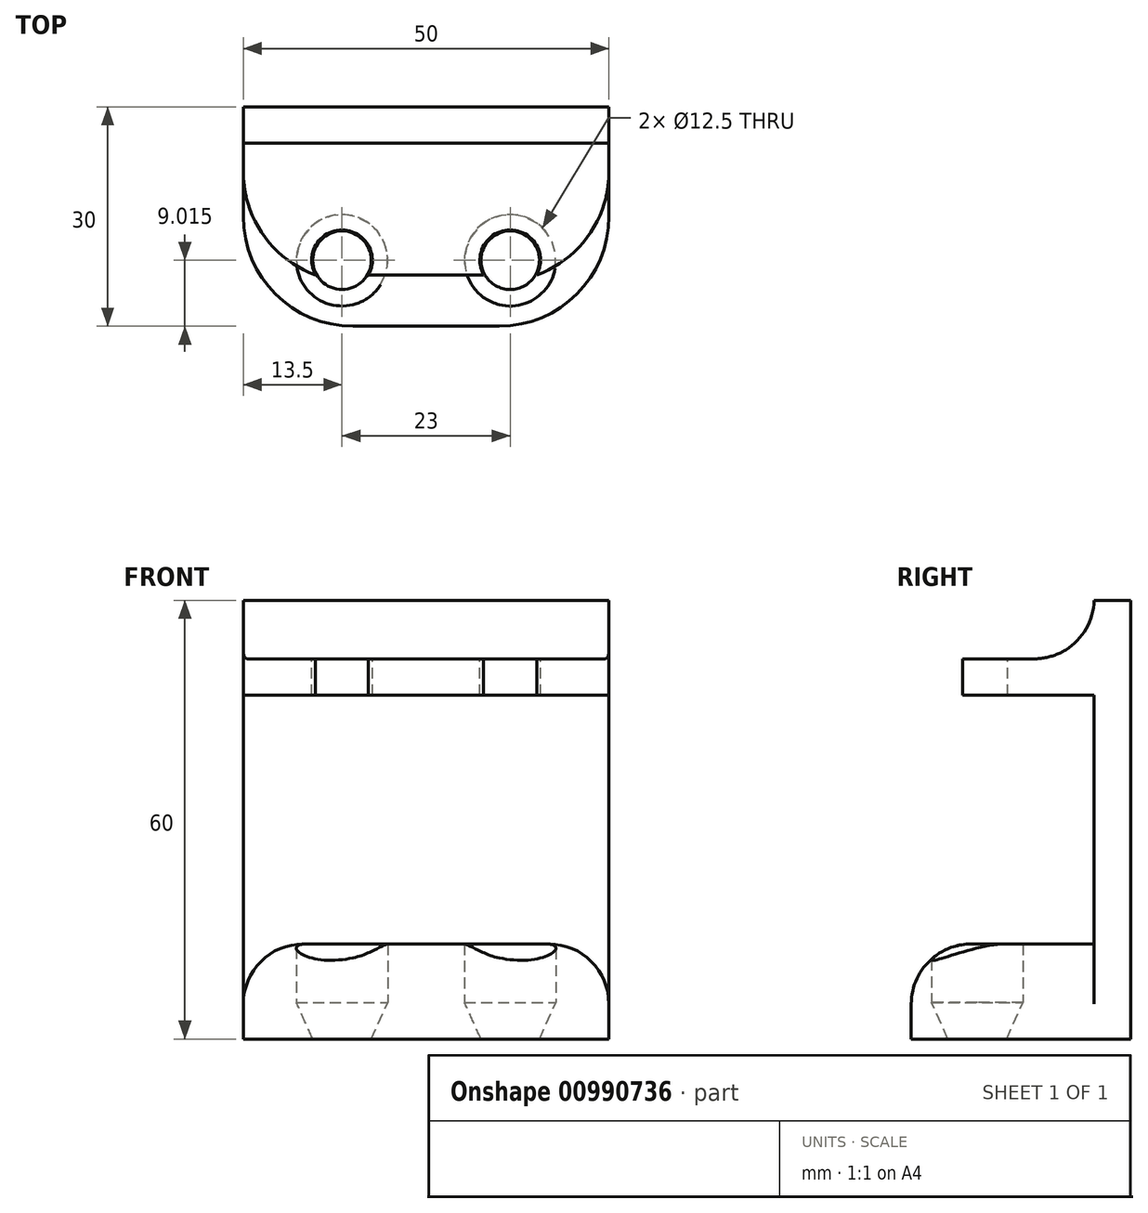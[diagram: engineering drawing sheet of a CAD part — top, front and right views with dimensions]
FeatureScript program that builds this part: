
annotation { "Feature Type Name" : "Feature", "Feature Type Description" : "" }
export const myFeature = defineFeature(function(context is Context, id is Id, definition is map)
    precondition{}
    {
        {
            var Q0;
            Q0=qCreatedBy(makeId("Front.planeOp"),FACE);
            var sketch = newSketch(context, id + "F0", { "sketchPlane" : qUnion([Q0])});
            skLineSegment(sketch, "E0.bottom", {"start": v(-25, 0) * mm, "end": v(25, 0) * mm});
            skLineSegment(sketch, "E0.top", {"start": v(-25, 60) * mm, "end": v(25, 60) * mm});
            skLineSegment(sketch, "E0.left", {"start": v(-25, 0) * mm, "end": v(-25, 60) * mm});
            skLineSegment(sketch, "E0.right", {"start": v(25, 0) * mm, "end": v(25, 60) * mm});
            skSolve(sketch);
        }
        {
            var Q0;
            Q0 = qSketchRegion(id + "F0", true);
            extrude(context, id + "F1", {"entities" : qUnion([Q0]), "depth" : 5 * mm, "offsetDistance" : 25 * mm});
        }
        {
            var Q0;
            Q0=makeQuery(id+"F1.opExtrude","CAP_FACE",FACE,{"disambiguationData":[OSD([sQuery(id+"F0.wireOp",EDGE,"E0.bottom"),sQuery(id+"F0.wireOp",EDGE,"E0.top"),sQuery(id+"F0.wireOp",EDGE,"E0.left"),sQuery(id+"F0.wireOp",EDGE,"E0.right")])],"isStart":false});
            var sketch = newSketch(context, id + "F2", { "sketchPlane" : qUnion([Q0])});
            skLineSegment(sketch, "E1.bottom", {"start": v(-25, 0) * mm, "end": v(25, 0) * mm});
            skLineSegment(sketch, "E1.top", {"start": v(-25, 5) * mm, "end": v(25, 5) * mm});
            skLineSegment(sketch, "E1.left", {"start": v(-25, 0) * mm, "end": v(-25, 5) * mm});
            skLineSegment(sketch, "E1.right", {"start": v(25, 0) * mm, "end": v(25, 5) * mm});
            skSolve(sketch);
        }
        {
            var Q0;
            Q0 = qSketchRegion(id + "F2", true);
            extrude(context, id + "F3", {"entities" : qUnion([Q0]), "operationType" : NewBodyOperationType.ADD, "depth" : 25 * mm, "offsetDistance" : 25 * mm});
        }
        {
            var Q0;
            Q0=makeQuery(id+"F1.opExtrude","CAP_FACE",FACE,{"disambiguationData":[OSD([sQuery(id+"F0.wireOp",EDGE,"E0.bottom"),sQuery(id+"F0.wireOp",EDGE,"E0.top"),sQuery(id+"F0.wireOp",EDGE,"E0.left"),sQuery(id+"F0.wireOp",EDGE,"E0.right")])],"isStart":false});
            var sketch = newSketch(context, id + "F4", { "sketchPlane" : qUnion([Q0])});
            skLineSegment(sketch, "E2.bottom", {"start": v(-25, 47) * mm, "end": v(25, 47) * mm});
            skLineSegment(sketch, "E2.top", {"start": v(-25, 52) * mm, "end": v(25, 52) * mm});
            skLineSegment(sketch, "E2.left", {"start": v(-25, 47) * mm, "end": v(-25, 52) * mm});
            skLineSegment(sketch, "E2.right", {"start": v(25, 47) * mm, "end": v(25, 52) * mm});
            skSolve(sketch);
        }
        {
            var Q0;
            Q0 = qSketchRegion(id + "F4", true);
            extrude(context, id + "F5", {"entities" : qUnion([Q0]), "operationType" : NewBodyOperationType.ADD, "depth" : 18 * mm, "offsetDistance" : 25 * mm});
        }
        {
            var Q0;
            Q0=makeQuery(id+"F3.opExtrude","SWEPT_FACE",FACE,{"disambiguationData":[OSD([sQuery(id+"F2.wireOp",EDGE,"E1.top")])]});
            var sketch = newSketch(context, id + "F6", { "sketchPlane" : qUnion([Q0])});
            skCircle(sketch, "E3", {"center": v(-11.5, -20.98) * mm, "radius": 6.25 * mm});
            skCircle(sketch, "E4", {"center": v(11.5, -20.98) * mm, "radius": 6.25 * mm});
            skSolve(sketch);
        }
        {
            var Q0;
            Q0=makeQuery(id+"F5.opExtrude","SWEPT_FACE",FACE,{"disambiguationData":[OSD([sQuery(id+"F4.wireOp",EDGE,"E2.top")])]});
            var sketch = newSketch(context, id + "F7", { "sketchPlane" : qUnion([Q0])});
            skCircle(sketch, "E5", {"center": v(-11.5, -20.98) * mm, "radius": 4.15 * mm});
            skCircle(sketch, "E6", {"center": v(11.5, -20.98) * mm, "radius": 4.15 * mm});
            skSolve(sketch);
        }
        {
            var Q0;
            Q0 = qSketchRegion(id + "F7", true);
            extrude(context, id + "F8", {"entities" : qUnion([Q0]), "operationType" : NewBodyOperationType.REMOVE, "oppositeDirection" : true, "depth" : 25 * mm, "offsetDistance" : 25 * mm});
        }
        {
            var Q0;
            Q0=makeQuery(id+"F3.opExtrude","CAP_EDGE",EDGE,{"disambiguationData":[OSD([sQuery(id+"F2.wireOp",EDGE,"E1.right")])],"isStart":false});
            var Q1;
            Q1=makeQuery(id+"F3.opExtrude","CAP_EDGE",EDGE,{"disambiguationData":[OSD([sQuery(id+"F2.wireOp",EDGE,"E1.left")])],"isStart":false});
            var Q2;
            Q2=makeQuery(id+"F5.opExtrude","CAP_EDGE",EDGE,{"disambiguationData":[OSD([sQuery(id+"F4.wireOp",EDGE,"E2.left")])],"isStart":false});
            var Q3;
            Q3=makeQuery(id+"F5.opExtrude","CAP_EDGE",EDGE,{"disambiguationData":[OSD([sQuery(id+"F4.wireOp",EDGE,"E2.right")])],"isStart":false});
            fillet(context, id + "F9", {"entities" : qUnion([Q0, Q1, Q2, Q3]), "radius" : 15 * mm, "tangentPropagation" : true, "allowEdgeOverflow" : false});
        }
        {
            var Q0;
            Q0=makeQuery(id+"F3.boolean.opBoolean","MERGE",FACE,{"derivedFrom":[makeQuery(id+"F1.opExtrude","SWEPT_FACE",FACE,{"disambiguationData":[OSD([sQuery(id+"F0.wireOp",EDGE,"E0.bottom")])]}),makeQuery(id+"F3.opExtrude","SWEPT_FACE",FACE,{"disambiguationData":[OSD([sQuery(id+"F2.wireOp",EDGE,"E1.bottom")])]})]});
            var sketch = newSketch(context, id + "F10", { "sketchPlane" : qUnion([Q0])});
            skCircle(sketch, "E7", {"center": v(-11.5, 20.98) * mm, "radius": 4 * mm});
            skCircle(sketch, "E8", {"center": v(11.5, 20.98) * mm, "radius": 4 * mm});
            skSolve(sketch);
        }
        {
            var Q1;
            Q1=makeQuery(id+"F6.imprint","IMPRINT",FACE,{"disambiguationData":[TD([[makeQuery(id+"F6.imprint","IMPRINT",EDGE,{"derivedFrom":sQuery(id+"F6.wireOp",EDGE,"E3")}),1.0]])]});
            var Q2;
            Q2=makeQuery(id+"F10.imprint","IMPRINT",FACE,{"disambiguationData":[TD([[makeQuery(id+"F10.imprint","IMPRINT",EDGE,{"derivedFrom":sQuery(id+"F10.wireOp",EDGE,"E7")}),1.0]])]});
            loft(context, id + "F11", {"operationType" : NewBodyOperationType.REMOVE, "sheetProfilesArray" : [{ "sheetProfileEntities" : qUnion([Q1]) }, { "sheetProfileEntities" : qUnion([Q2]) }]});
        }
        {
            var Q1;
            Q1=makeQuery(id+"F6.imprint","IMPRINT",FACE,{"disambiguationData":[TD([[makeQuery(id+"F6.imprint","IMPRINT",EDGE,{"derivedFrom":sQuery(id+"F6.wireOp",EDGE,"E4")}),1.0]])]});
            var Q2;
            Q2=makeQuery(id+"F10.imprint","IMPRINT",FACE,{"disambiguationData":[TD([[makeQuery(id+"F10.imprint","IMPRINT",EDGE,{"derivedFrom":sQuery(id+"F10.wireOp",EDGE,"E8")}),1.0]])]});
            var Q3;
            Q3=sQuery(id+"F10.wireOp",EDGE,"E8");
            var Q4;
            Q4=sQuery(id+"F6.wireOp",EDGE,"E4");
            loft(context, id + "F12", {"operationType" : NewBodyOperationType.REMOVE, "sheetProfilesArray" : [{ "sheetProfileEntities" : qUnion([Q1]) }, { "sheetProfileEntities" : qUnion([Q2]) }], "wireProfilesArray" : [{ "wireProfileEntities" : qUnion([Q3]) }, { "wireProfileEntities" : qUnion([Q4]) }]});
        }
        {
            var Q0;
            Q0=makeQuery(id+"F6.imprint","IMPRINT",FACE,{"disambiguationData":[TD([[makeQuery(id+"F6.imprint","IMPRINT",EDGE,{"derivedFrom":sQuery(id+"F6.wireOp",EDGE,"E3")}),-1.0]])]});
            extrude(context, id + "F13", {"entities" : qUnion([Q0]), "operationType" : NewBodyOperationType.ADD, "depth" : 8 * mm, "offsetDistance" : 25 * mm});
        }
        {
            var Q0;
            {var subQ0=sQuery(id+"F2.wireOp",EDGE,"E1.top");var subQ1=sQuery(id+"F2.wireOp",EDGE,"E1.left");var subQ2=sQuery(id+"F0.wireOp",EDGE,"E0.left");Q0=makeQuery(id+"F13.opExtrude","SWEPT_EDGE",EDGE,{"disambiguationData":[OSD([subQ2,subQ0,subQ1]),TDD([makeQuery(id+"F6.imprint","INTERSECT",VERTEX,{"derivedFrom":[makeQuery(id+"F3.opExtrude","SWEPT_EDGE",EDGE,{"disambiguationData":[OSD([subQ2,subQ0,subQ1])]}),makeQuery(id+"F3.opExtrude","CAP_EDGE",EDGE,{"disambiguationData":[OSD([subQ0])],"isStart":false})]})])]});}
            var Q1;
            {var subQ0=sQuery(id+"F2.wireOp",EDGE,"E1.top");var subQ1=sQuery(id+"F2.wireOp",EDGE,"E1.right");var subQ2=sQuery(id+"F0.wireOp",EDGE,"E0.right");Q1=makeQuery(id+"F13.opExtrude","SWEPT_EDGE",EDGE,{"disambiguationData":[OSD([subQ2,subQ0,subQ1]),TDD([makeQuery(id+"F6.imprint","INTERSECT",VERTEX,{"derivedFrom":[makeQuery(id+"F3.opExtrude","SWEPT_EDGE",EDGE,{"disambiguationData":[OSD([subQ2,subQ0,subQ1])]}),makeQuery(id+"F3.opExtrude","CAP_EDGE",EDGE,{"disambiguationData":[OSD([subQ0])],"isStart":false})]})])]});}
            fillet(context, id + "F14", {"entities" : qUnion([Q0, Q1]), "radius" : 15 * mm, "tangentPropagation" : true, "allowEdgeOverflow" : false});
        }
        {
            var Q0;
            Q0=makeQuery(id+"F5.opExtrude","CAP_EDGE",EDGE,{"disambiguationData":[OSD([sQuery(id+"F4.wireOp",EDGE,"E2.bottom")])],"isStart":true});
            var Q1;
            {var subQ0=sQuery(id+"F2.wireOp",EDGE,"E1.top");Q1=makeQuery(id+"F13.opExtrude","CAP_EDGE",EDGE,{"disambiguationData":[OSD([subQ0]),TDD([makeQuery(id+"F6.imprint","IMPRINT",EDGE,{"derivedFrom":makeQuery(id+"F3.opExtrude","CAP_EDGE",EDGE,{"disambiguationData":[OSD([subQ0])],"isStart":true})})])],"isStart":false});}
            var Q2;
            Q2=makeQuery(id+"F5.opExtrude","CAP_EDGE",EDGE,{"disambiguationData":[OSD([sQuery(id+"F4.wireOp",EDGE,"E2.top")])],"isStart":true});
            fillet(context, id + "F15", {"entities" : qUnion([Q0, Q1, Q2]), "radius" : 8.2 * mm, "tangentPropagation" : true, "allowEdgeOverflow" : false});
        }
    });
